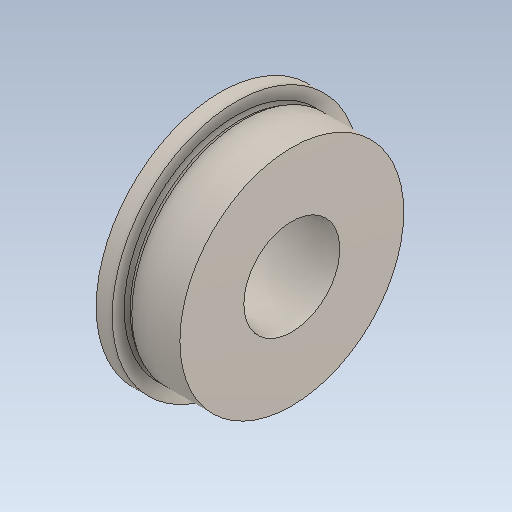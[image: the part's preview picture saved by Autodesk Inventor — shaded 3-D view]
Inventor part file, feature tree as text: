
AUTODESK INVENTOR PART (.ipt)
format: ipt  version: 2020 (Build 240168000, 168)  size: 156,672 bytes
history: native  units: in
note: dims shown in document units (in); Inventor stores cm internally (conversion verified against a paired STEP export)
features: revolve x1
ambient origin geometry x8: Origin, YZ Plane, XZ Plane, XY Plane, X Axis, Y Axis, Z Axis, Center Point
bodies: Solid1 (feature_tree)
feature tree (1):
  revolve  "Revolve1"  [1 undecoded]
note: 1 required parameter value undecoded (feature->parameter linkage not recoverable at this tier; creation-order binding heuristic only, values carry confidence <= 0.55)
